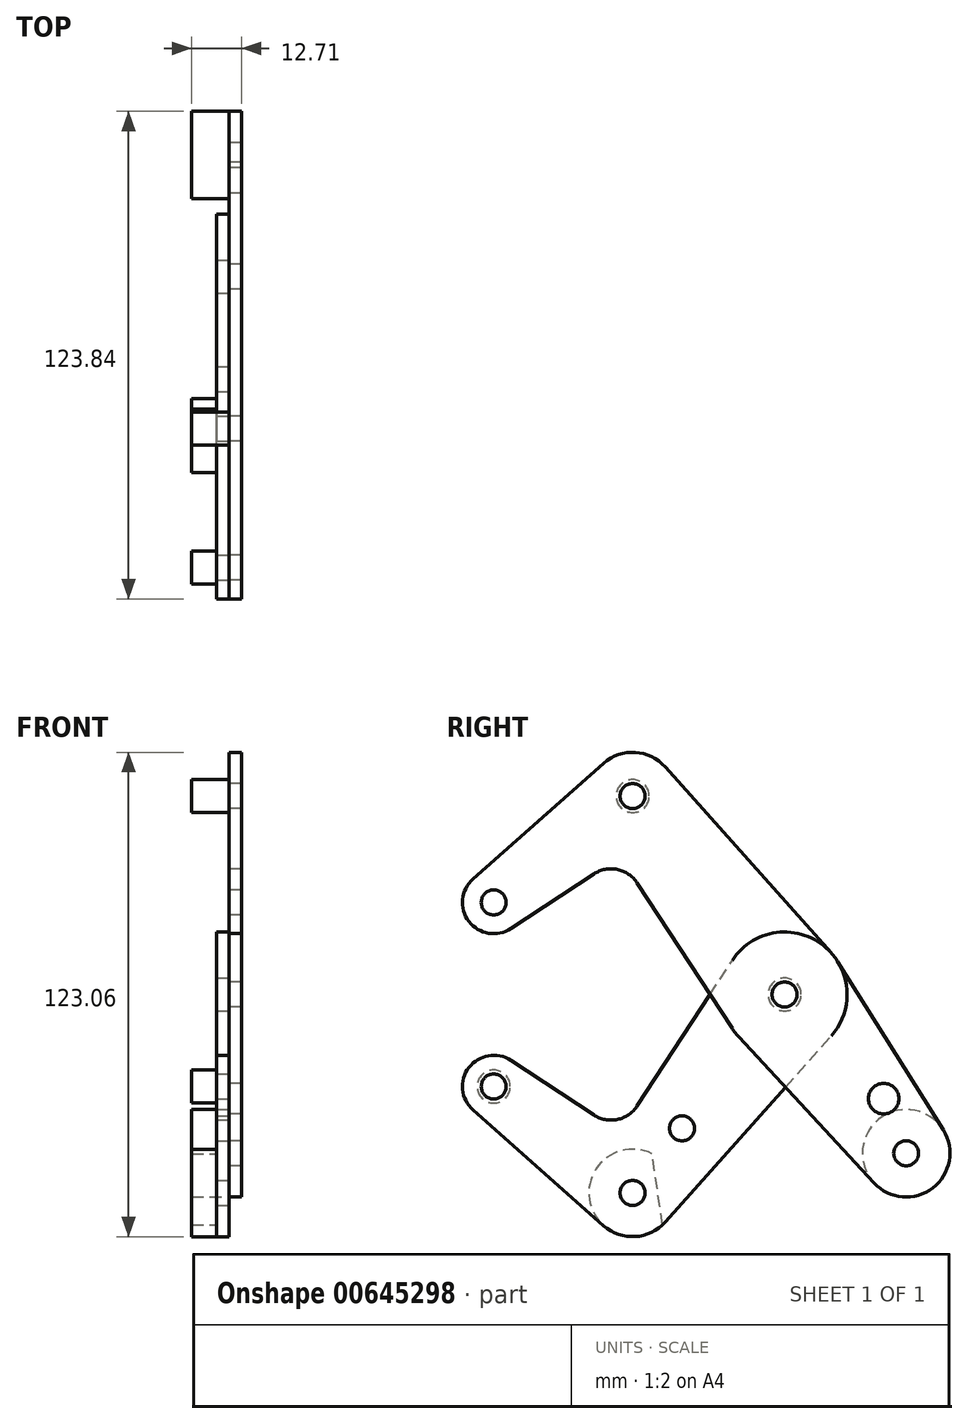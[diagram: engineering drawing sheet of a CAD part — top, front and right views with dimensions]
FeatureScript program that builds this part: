
annotation { "Feature Type Name" : "Feature", "Feature Type Description" : "" }
export const myFeature = defineFeature(function(context is Context, id is Id, definition is map)
    precondition{}
    {
        {
            var Q0;
            Q0=qCreatedBy(makeId("Right.planeOp"),FACE);
            var sketch = newSketch(context, id + "F0", { "sketchPlane" : qUnion([Q0])});
            skCircle(sketch, "E0", {"center": v(-73.9, 23.39) * mm, "radius": 7.94 * mm});
            skCircle(sketch, "E1", {"center": v(-38.61, 50.41) * mm, "radius": 11.11 * mm});
            skCircle(sketch, "E2", {"center": v(0, 0) * mm, "radius": 15.88 * mm});
            skCircle(sketch, "E3", {"center": v(30.89, -40.33) * mm, "radius": 11.11 * mm});
            skLineSegment(sketch, "E4", {"start": v(-73.9, 23.39) * mm, "end": v(-38.61, 50.41) * mm, "construction": true});
            skLineSegment(sketch, "E5", {"start": v(-38.61, 50.41) * mm, "end": v(0, 0) * mm, "construction": true});
            skLineSegment(sketch, "E6", {"start": v(0, 0) * mm, "end": v(30.89, -40.33) * mm, "construction": true});
            skCircle(sketch, "E7", {"center": v(30.89, -40.33) * mm, "radius": 3.18 * mm});
            skCircle(sketch, "E8", {"center": v(0, 0) * mm, "radius": 3.18 * mm});
            skCircle(sketch, "E9", {"center": v(-38.61, 50.41) * mm, "radius": 3.18 * mm});
            skCircle(sketch, "E10", {"center": v(-73.9, 23.39) * mm, "radius": 3.18 * mm});
            skCircle(sketch, "E11", {"center": v(0, 0) * mm, "radius": 4.2 * mm});
            skCircle(sketch, "E12", {"center": v(25.16, -26.47) * mm, "radius": 3.88 * mm});
            skLineSegment(sketch, "E13", {"start": v(-79.16, 29.33) * mm, "end": v(-45.98, 58.73) * mm});
            skLineSegment(sketch, "E14.MirrorCS", {"start": v(-69.54, 16.76) * mm, "end": v(-48.48, 30.61) * mm});
            skLineSegment(sketch, "E15", {"start": v(-30.32, 57.81) * mm, "end": v(11.84, 10.57) * mm});
            skLineSegment(sketch, "E16.MirrorCS", {"start": v(-47.91, 44.34) * mm, "end": v(-47.46, 43.64) * mm});
            skLineSegment(sketch, "E17", {"start": v(13.45, 8.43) * mm, "end": v(40.3, -34.43) * mm});
            skLineSegment(sketch, "E18.MirrorCS", {"start": v(-11.64, -10.8) * mm, "end": v(22.74, -47.88) * mm});
            skPoint(sketch, "E19.orphan", {"position": v(-32.5, 41.13) * mm});
            skLineSegment(sketch, "E20.trimOffspring", {"start": v(-37.45, 28.32) * mm, "end": v(-13.3, -8.68) * mm});
            skArc(sketch, "E21", {"start": v(-37.45, 28.32) * mm, "mid": v(-42.5, 31.76) * mm, "end": v(-48.48, 30.61) * mm});
            skCircle(sketch, "E22", {"center": v(-38.61, -50.41) * mm, "radius": 11.11 * mm});
            skCircle(sketch, "E23", {"center": v(-73.9, -23.39) * mm, "radius": 7.94 * mm});
            skLineSegment(sketch, "E24", {"start": v(-73.9, 23.39) * mm, "end": v(-73.9, -23.39) * mm, "construction": true});
            skLineSegment(sketch, "E25", {"start": v(-73.9, -23.39) * mm, "end": v(-38.61, -50.41) * mm, "construction": true});
            skLineSegment(sketch, "E26", {"start": v(-38.61, -50.41) * mm, "end": v(0, 0) * mm, "construction": true});
            skCircle(sketch, "E27", {"center": v(-26.05, -34.02) * mm, "radius": 3.18 * mm});
            skLineSegment(sketch, "E28", {"start": v(-79.16, -29.33) * mm, "end": v(-45.98, -58.73) * mm});
            skLineSegment(sketch, "E29", {"start": v(-30.32, -57.81) * mm, "end": v(11.84, -10.57) * mm});
            skLineSegment(sketch, "E30.MirrorCS", {"start": v(-69.54, -16.76) * mm, "end": v(-48.48, -30.61) * mm});
            skLineSegment(sketch, "E31.MirrorCS", {"start": v(-47.91, -44.34) * mm, "end": v(-47.46, -43.64) * mm});
            skLineSegment(sketch, "E32.trimOffspring", {"start": v(-37.45, -28.32) * mm, "end": v(-13.3, 8.68) * mm});
            skPoint(sketch, "E33.orphan", {"position": v(-32.5, -41.13) * mm});
            skArc(sketch, "E34", {"start": v(-37.45, -28.32) * mm, "mid": v(-42.5, -31.76) * mm, "end": v(-48.48, -30.61) * mm});
            skCircle(sketch, "E35", {"center": v(-73.9, -23.39) * mm, "radius": 3.18 * mm});
            skCircle(sketch, "E36", {"center": v(-38.61, -50.41) * mm, "radius": 3.18 * mm});
            skCircle(sketch, "E37", {"center": v(-73.9, -23.39) * mm, "radius": 4.2 * mm});
            skLineSegment(sketch, "E38", {"start": v(-38.61, -50.41) * mm, "end": v(30.89, -40.33) * mm, "construction": true});
            skSolve(sketch);
        }
        {
            var Q0;
            Q0=makeQuery(id+"F0.imprint","IMPRINT",FACE,{"disambiguationData":[TD([[makeQuery(id+"F0.imprint","IMPRINT",EDGE,{"derivedFrom":sQuery(id+"F0.wireOp",EDGE,"E10")}),-1.0]])]});
            var Q1;
            {var subQ7=sQuery(id+"F0.wireOp",EDGE,"E13");Q1=makeQuery(id+"F0.imprint","IMPRINT",FACE,{"disambiguationData":[TD([[makeQuery(id+"F0.imprint","IMPRINT",EDGE,{"derivedFrom":subQ7}),-1.0]])]});}
            var Q2;
            Q2=makeQuery(id+"F0.imprint","IMPRINT",FACE,{"disambiguationData":[TD([[makeQuery(id+"F0.imprint","IMPRINT",EDGE,{"derivedFrom":sQuery(id+"F0.wireOp",EDGE,"E9")}),-1.0]])]});
            var Q3;
            Q3=makeQuery(id+"F0.imprint","IMPRINT",FACE,{"disambiguationData":[TD([[makeQuery(id+"F0.imprint","IMPRINT",EDGE,{"derivedFrom":sQuery(id+"F0.wireOp",EDGE,"E11")}),-1.0]])]});
            var Q4;
            {var subQ0=sQuery(id+"F0.wireOp",EDGE,"E12");Q4=makeQuery(id+"F0.imprint","IMPRINT",FACE,{"disambiguationData":[TD([[makeQuery(id+"F0.imprint","IMPRINT",EDGE,{"derivedFrom":subQ0}),-1.0]])]});}
            var Q5;
            Q5=makeQuery(id+"F0.imprint","IMPRINT",FACE,{"disambiguationData":[TD([[makeQuery(id+"F0.imprint","IMPRINT",EDGE,{"derivedFrom":sQuery(id+"F0.wireOp",EDGE,"E7")}),-1.0]])]});
            var Q6;
            {var subQ0=sQuery(id+"F0.wireOp",EDGE,"E18.MirrorCS");var subQ1=sQuery(id+"F0.wireOp",EDGE,"E2");var subQ2=makeQuery(id+"F0.imprint","INTERSECT",VERTEX,{"derivedFrom":[subQ1,subQ0]});Q6=makeQuery(id+"F0.imprint","IMPRINT",FACE,{"disambiguationData":[TD([[makeQuery(id+"F0.imprint","IMPRINT",EDGE,{"disambiguationData":[TD([[subQ2,-1.0]])],"derivedFrom":subQ1}),-1.0]])]});}
            var Q7;
            {var subQ0=sQuery(id+"F0.wireOp",EDGE,"E20.trimOffspring");var subQ1=sQuery(id+"F0.wireOp",EDGE,"E2");var subQ2=makeQuery(id+"F0.imprint","INTERSECT",VERTEX,{"derivedFrom":[subQ1,subQ0]});Q7=makeQuery(id+"F0.imprint","IMPRINT",FACE,{"disambiguationData":[TD([[makeQuery(id+"F0.imprint","IMPRINT",EDGE,{"disambiguationData":[TD([[subQ2,1.0]])],"derivedFrom":subQ1}),-1.0]])]});}
            var Q8;
            Q8=makeQuery(id+"F0.imprint","IMPRINT",FACE,{"disambiguationData":[TD([[makeQuery(id+"F0.imprint","IMPRINT",EDGE,{"derivedFrom":sQuery(id+"F0.wireOp",EDGE,"E8")}),-1.0]])]});
            extrude(context, id + "F1", {"entities" : qUnion([Q0, Q1, Q2, Q3, Q4, Q5, Q6, Q7, Q8]), "depth" : 3.17 * mm, "offsetDistance" : 25.4 * mm});
        }
        {
            var Q0;
            Q0=makeQuery(id+"F0.imprint","IMPRINT",FACE,{"disambiguationData":[TD([[makeQuery(id+"F0.imprint","IMPRINT",EDGE,{"derivedFrom":sQuery(id+"F0.wireOp",EDGE,"E27")}),-1.0]])]});
            var Q1;
            Q1=makeQuery(id+"F0.imprint","IMPRINT",FACE,{"disambiguationData":[TD([[makeQuery(id+"F0.imprint","IMPRINT",EDGE,{"derivedFrom":sQuery(id+"F0.wireOp",EDGE,"E36")}),-1.0]])]});
            var Q2;
            Q2=makeQuery(id+"F0.imprint","IMPRINT",FACE,{"disambiguationData":[TD([[makeQuery(id+"F0.imprint","IMPRINT",EDGE,{"derivedFrom":sQuery(id+"F0.wireOp",EDGE,"E35")}),-1.0]])]});
            var Q3;
            Q3=makeQuery(id+"F0.imprint","IMPRINT",FACE,{"disambiguationData":[TD([[makeQuery(id+"F0.imprint","IMPRINT",EDGE,{"derivedFrom":sQuery(id+"F0.wireOp",EDGE,"E11")}),-1.0]])]});
            var Q4;
            {var subQ0=sQuery(id+"F0.wireOp",EDGE,"E20.trimOffspring");var subQ1=sQuery(id+"F0.wireOp",EDGE,"E2");var subQ2=makeQuery(id+"F0.imprint","INTERSECT",VERTEX,{"derivedFrom":[subQ1,subQ0]});Q4=makeQuery(id+"F0.imprint","IMPRINT",FACE,{"disambiguationData":[TD([[makeQuery(id+"F0.imprint","IMPRINT",EDGE,{"disambiguationData":[TD([[subQ2,1.0]])],"derivedFrom":subQ1}),-1.0]])]});}
            var Q5;
            {var subQ0=sQuery(id+"F0.wireOp",EDGE,"E18.MirrorCS");var subQ1=sQuery(id+"F0.wireOp",EDGE,"E2");var subQ2=makeQuery(id+"F0.imprint","INTERSECT",VERTEX,{"derivedFrom":[subQ1,subQ0]});Q5=makeQuery(id+"F0.imprint","IMPRINT",FACE,{"disambiguationData":[TD([[makeQuery(id+"F0.imprint","IMPRINT",EDGE,{"disambiguationData":[TD([[subQ2,-1.0]])],"derivedFrom":subQ1}),-1.0]])]});}
            var Q6;
            Q6=makeQuery(id+"F0.imprint","IMPRINT",FACE,{"disambiguationData":[TD([[makeQuery(id+"F0.imprint","IMPRINT",EDGE,{"derivedFrom":sQuery(id+"F0.wireOp",EDGE,"E37")}),-1.0]])]});
            extrude(context, id + "F2", {"entities" : qUnion([Q0, Q1, Q2, Q3, Q4, Q5, Q6]), "oppositeDirection" : true, "depth" : 3.17 * mm, "offsetDistance" : 25.4 * mm});
        }
        {
            var Q0;
            Q0=makeQuery(id+"F1.opExtrude","CAP_FACE",FACE,{"disambiguationData":[OSD([sQuery(id+"F0.wireOp",EDGE,"E0"),sQuery(id+"F0.wireOp",EDGE,"E1"),sQuery(id+"F0.wireOp",EDGE,"E2"),sQuery(id+"F0.wireOp",EDGE,"E3"),sQuery(id+"F0.wireOp",EDGE,"E7"),sQuery(id+"F0.wireOp",EDGE,"E8"),sQuery(id+"F0.wireOp",EDGE,"E9"),sQuery(id+"F0.wireOp",EDGE,"E10"),sQuery(id+"F0.wireOp",EDGE,"E12"),sQuery(id+"F0.wireOp",EDGE,"E13"),sQuery(id+"F0.wireOp",EDGE,"E14.MirrorCS"),sQuery(id+"F0.wireOp",EDGE,"E15"),sQuery(id+"F0.wireOp",EDGE,"E17"),sQuery(id+"F0.wireOp",EDGE,"E18.MirrorCS"),sQuery(id+"F0.wireOp",EDGE,"E20.trimOffspring"),sQuery(id+"F0.wireOp",EDGE,"E21")])],"isStart":false});
            var sketch = newSketch(context, id + "F3", { "sketchPlane" : qUnion([Q0])});
            skCircle(sketch, "E39.0", {"center": v(30.89, -40.33) * mm, "radius": 11.11 * mm});
            skCircle(sketch, "E39.1", {"center": v(0, 0) * mm, "radius": 4.2 * mm});
            skCircle(sketch, "E40", {"center": v(-38.61, 50.41) * mm, "radius": 4.2 * mm});
            skSolve(sketch);
        }
        {
            var Q0;
            Q0=makeQuery(id+"F0.imprint","IMPRINT",FACE,{"disambiguationData":[TD([[makeQuery(id+"F0.imprint","IMPRINT",EDGE,{"derivedFrom":sQuery(id+"F0.wireOp",EDGE,"E27")}),-1.0]])]});
            var sketch = newSketch(context, id + "F4", { "sketchPlane" : qUnion([Q0])});
            skCircle(sketch, "E41.0", {"center": v(-38.61, -50.41) * mm, "radius": 11.11 * mm});
            skLineSegment(sketch, "E42", {"start": v(-33.64, -40.48) * mm, "end": v(-31.02, -58.53) * mm});
            skCircle(sketch, "E43.0", {"center": v(-73.9, -23.39) * mm, "radius": 4.2 * mm});
            skCircle(sketch, "E44.0", {"center": v(30.89, -40.33) * mm, "radius": 3.18 * mm});
            skLineSegment(sketch, "E45", {"start": v(-32.33, -49.5) * mm, "end": v(30.89, -40.33) * mm, "construction": true});
            skSolve(sketch);
        }
        {
            var Q0;
            Q0=qCreatedBy(makeId("Right.planeOp"),FACE);
            cPlane(context, id + "F5", {"entities" : qUnion([Q0]), "cplaneType" : CPlaneType.OFFSET, "offset" : 9.52 * mm, "oppositeDirection" : true, "width" : 152.4 * mm, "height" : 152.4 * mm});
        }
        {
            var Q0;
            {var subQ2=sQuery(id+"F4.wireOp",EDGE,"E42");Q0=makeQuery(id+"F4.imprint","IMPRINT",FACE,{"disambiguationData":[TD([[makeQuery(id+"F4.imprint","IMPRINT",EDGE,{"derivedFrom":subQ2}),-1.0]])]});}
            var Q1;
            Q1=makeQuery(id+"F3.imprint","IMPRINT",FACE,{"disambiguationData":[TD([[makeQuery(id+"F3.imprint","IMPRINT",EDGE,{"derivedFrom":makeQuery(id+"F1.opExtrude","CAP_EDGE",EDGE,{"disambiguationData":[OSD([sQuery(id+"F0.wireOp",EDGE,"E7")])],"isStart":false})}),-1.0]])]});
            var Q2;
            Q2=makeQuery(id+"F4.imprint","IMPRINT",FACE,{"disambiguationData":[TD([[makeQuery(id+"F4.imprint","IMPRINT",EDGE,{"derivedFrom":sQuery(id+"F4.wireOp",EDGE,"E43.0")}),1.0]])]});
            var Q3;
            Q3=makeQuery(id+"F3.imprint","IMPRINT",FACE,{"disambiguationData":[TD([[makeQuery(id+"F3.imprint","IMPRINT",EDGE,{"derivedFrom":sQuery(id+"F3.wireOp",EDGE,"E40")}),1.0]])]});
            var Q4;
            Q4=makeQuery(id+"F3.imprint","IMPRINT",FACE,{"disambiguationData":[TD([[makeQuery(id+"F3.imprint","IMPRINT",EDGE,{"derivedFrom":makeQuery(id+"F1.opExtrude","CAP_EDGE",EDGE,{"disambiguationData":[OSD([sQuery(id+"F0.wireOp",EDGE,"E9")])],"isStart":false})}),1.0]])]});
            var Q5;
            Q5=makeQuery(id+"F3.imprint","IMPRINT",FACE,{"disambiguationData":[TD([[makeQuery(id+"F3.imprint","IMPRINT",EDGE,{"derivedFrom":makeQuery(id+"F1.opExtrude","CAP_EDGE",EDGE,{"disambiguationData":[OSD([sQuery(id+"F0.wireOp",EDGE,"E7")])],"isStart":false})}),1.0]])]});
            var Q6;
            Q6=qCreatedBy(id+"F5.planeOp",FACE);
            extrude(context, id + "F6", {"entities" : qUnion([Q0, Q1, Q2, Q3, Q4, Q5]), "endBound" : BoundingType.UP_TO_SURFACE, "oppositeDirection" : true, "depth" : 25.4 * mm, "endBoundEntityFace" : qUnion([Q6]), "offsetDistance" : 25.4 * mm});
        }
        {
            var Q0;
            Q0=makeQuery(id+"F1.opExtrude","SWEPT_BODY",BODY,{"disambiguationData":[OSD([sQuery(id+"F0.wireOp",EDGE,"E0"),sQuery(id+"F0.wireOp",EDGE,"E1"),sQuery(id+"F0.wireOp",EDGE,"E2"),sQuery(id+"F0.wireOp",EDGE,"E3"),sQuery(id+"F0.wireOp",EDGE,"E7"),sQuery(id+"F0.wireOp",EDGE,"E8"),sQuery(id+"F0.wireOp",EDGE,"E9"),sQuery(id+"F0.wireOp",EDGE,"E10"),sQuery(id+"F0.wireOp",EDGE,"E12"),sQuery(id+"F0.wireOp",EDGE,"E13"),sQuery(id+"F0.wireOp",EDGE,"E14.MirrorCS"),sQuery(id+"F0.wireOp",EDGE,"E15"),sQuery(id+"F0.wireOp",EDGE,"E17"),sQuery(id+"F0.wireOp",EDGE,"E18.MirrorCS"),sQuery(id+"F0.wireOp",EDGE,"E20.trimOffspring"),sQuery(id+"F0.wireOp",EDGE,"E21")])]});
            var Q1;
            Q1=makeQuery(id+"F2.opExtrude","SWEPT_BODY",BODY,{"disambiguationData":[OSD([sQuery(id+"F0.wireOp",EDGE,"E2"),sQuery(id+"F0.wireOp",EDGE,"E11"),sQuery(id+"F0.wireOp",EDGE,"E22"),sQuery(id+"F0.wireOp",EDGE,"E23"),sQuery(id+"F0.wireOp",EDGE,"E27"),sQuery(id+"F0.wireOp",EDGE,"E28"),sQuery(id+"F0.wireOp",EDGE,"E29"),sQuery(id+"F0.wireOp",EDGE,"E30.MirrorCS"),sQuery(id+"F0.wireOp",EDGE,"E32.trimOffspring"),sQuery(id+"F0.wireOp",EDGE,"E34"),sQuery(id+"F0.wireOp",EDGE,"E35"),sQuery(id+"F0.wireOp",EDGE,"E36")])]});
            var Q2;
            Q2=makeQuery(id+"F6.opExtrude","SWEPT_BODY",BODY,{"disambiguationData":[OSD([sQuery(id+"F3.wireOp",EDGE,"E40")])]});
            var Q3;
            Q3=makeQuery(id+"F6.opExtrude","SWEPT_BODY",BODY,{"disambiguationData":[OSD([sQuery(id+"F3.wireOp",EDGE,"E39.0")])]});
            var Q4;
            Q4=makeQuery(id+"F6.opExtrude","SWEPT_BODY",BODY,{"disambiguationData":[OSD([sQuery(id+"F4.wireOp",EDGE,"E41.0"),sQuery(id+"F4.wireOp",EDGE,"E42")])]});
            var Q5;
            Q5=makeQuery(id+"F6.opExtrude","SWEPT_BODY",BODY,{"disambiguationData":[OSD([sQuery(id+"F4.wireOp",EDGE,"E43.0")])]});
            booleanBodies(context, id + "F7", {"operationType" : BooleanOperationType.SUBTRACTION, "tools" : qUnion([Q0, Q1]), "targets" : qUnion([Q2, Q3, Q4, Q5]), "keepTools" : true});
        }
    });
